# Revit family: Haworth_Lighting-LIM_Y
name_source: partatom
category: Lighting Fixtures
revit_build: Autodesk Revit Architecture 2012 (Build: 20110309_2315)
units: mm (PartAtom-declared; Revit-internal decimal feet)

## types (1)
- Worksurface Mount
    Actual Height = 18 3/4"
    Actual Width = 26 1/2"
    Arm Length = 12 3/8"
    Assembly Code = D5020200
    Description = LIM Light
    LEED Data = www.haworth.com/_layouts/Haworth.ProductCatalog/Handlers/GetAsset.ashx/LIM-Brochure.pdf?cid=724&rid=652&type=Brochure
    Lamp Finish = Haworth - Metal - Brushed Aluminum
    Light Source Height = 13 13/16"
    Manufacturer = Haworth
    Model = LIM
    Post to Centerline = 3"
    Revision Number = 1
    Size = Verify Final Dim. w/ Haworth
    Sustainability Info = www.haworth.com/en-us/About-Us/Sustainability/Pages/Vision.aspx
    Table Thickness = 1 1/2"
    URL = www.haworth.com
    URL - Product = http://www.haworth.com
    Warranty = www.haworth.com/en-us/Products/Pages/Certifications.aspx
    Wattage Comments = 3 or 7.3 Watts; 120 Volt 60 Hertz

## geometry (parser evidence)
native form markers: Blend x2, Sweep x2
no freeform markers — native parametric forms only
